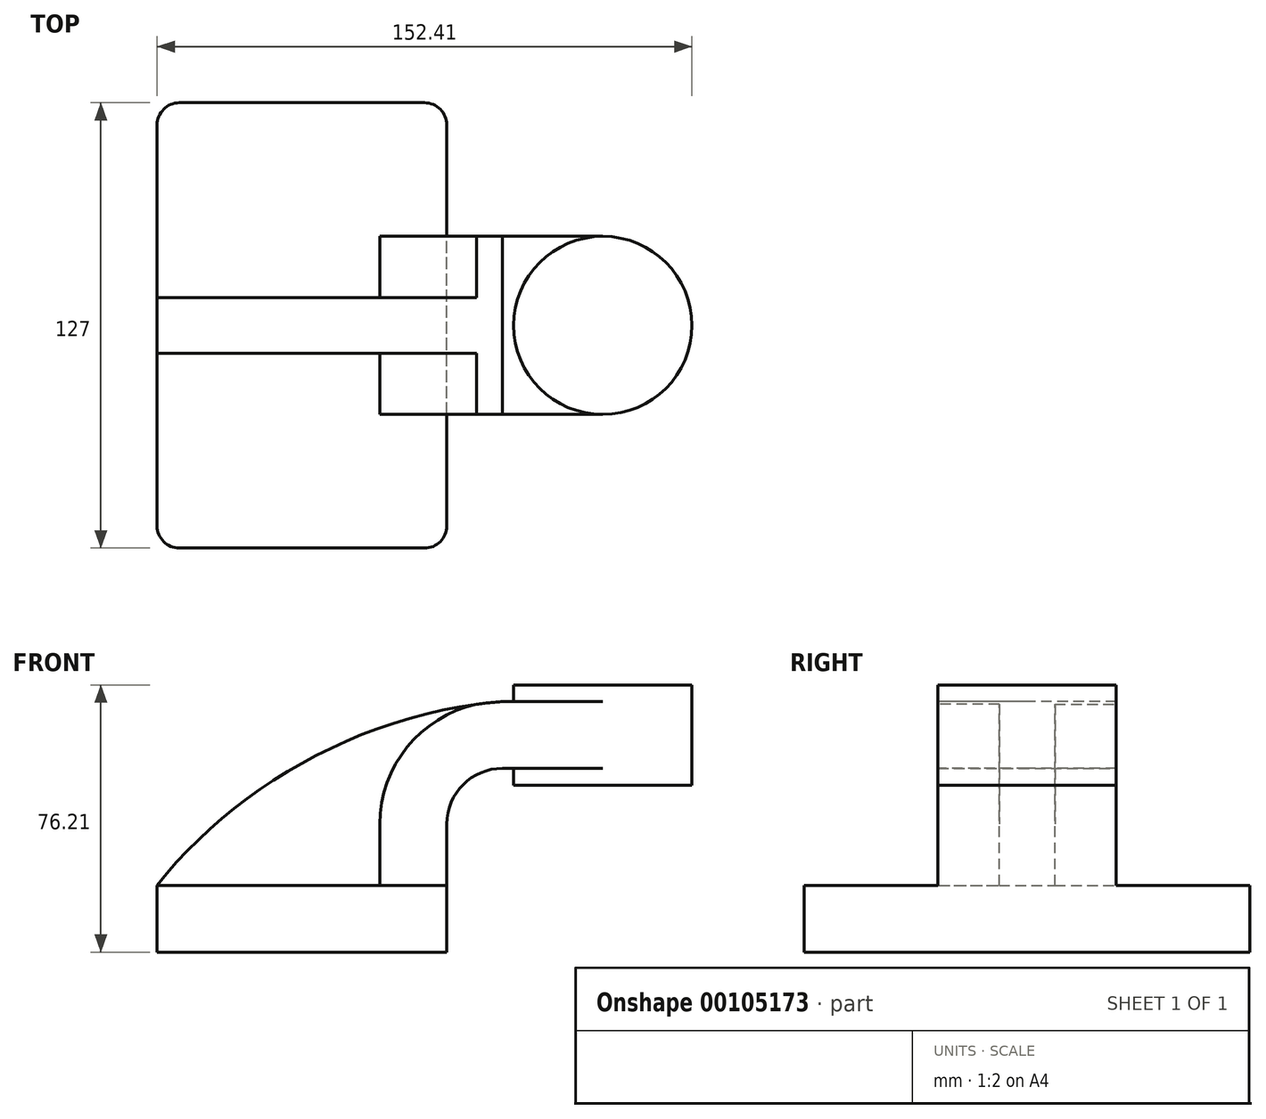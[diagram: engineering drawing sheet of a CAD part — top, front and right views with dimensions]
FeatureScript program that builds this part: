
annotation { "Feature Type Name" : "Feature", "Feature Type Description" : "" }
export const myFeature = defineFeature(function(context is Context, id is Id, definition is map)
    precondition{}
    {
        {
            var Q0;
            Q0=qCreatedBy(makeId("Front.planeOp"),FACE);
            var sketch = newSketch(context, id + "F0", { "sketchPlane" : qUnion([Q0])});
            skLineSegment(sketch, "E0.bottom", {"start": v(41.27, 9.53) * mm, "end": v(-41.28, 9.53) * mm});
            skLineSegment(sketch, "E0.top", {"start": v(41.28, -9.52) * mm, "end": v(-41.27, -9.52) * mm});
            skLineSegment(sketch, "E0.left", {"start": v(41.27, 9.53) * mm, "end": v(41.28, -9.52) * mm});
            skLineSegment(sketch, "E0.right", {"start": v(-41.28, 9.52) * mm, "end": v(-41.27, -9.52) * mm});
            skPoint(sketch, "E0.middle", {"position": v(0, 0) * mm});
            skLineSegment(sketch, "E1.bottom", {"start": v(111.12, 38.1) * mm, "end": v(60.32, 38.1) * mm});
            skLineSegment(sketch, "E1.top", {"start": v(111.12, 66.68) * mm, "end": v(60.32, 66.68) * mm});
            skLineSegment(sketch, "E1.left", {"start": v(111.12, 38.1) * mm, "end": v(111.12, 66.68) * mm});
            skLineSegment(sketch, "E1.right", {"start": v(60.32, 38.1) * mm, "end": v(60.32, 66.68) * mm});
            skPoint(sketch, "E1.middle", {"position": v(85.72, 52.39) * mm});
            skLineSegment(sketch, "E2", {"start": v(41.27, 9.53) * mm, "end": v(41.27, 27) * mm});
            skArc(sketch, "E3", {"start": v(41.27, 27) * mm, "mid": v(45.92, 38.23) * mm, "end": v(57.15, 42.88) * mm});
            skLineSegment(sketch, "E4", {"start": v(57.15, 42.88) * mm, "end": v(85.72, 42.88) * mm});
            skLineSegment(sketch, "E5.0", {"start": v(57.15, 61.93) * mm, "end": v(85.72, 61.93) * mm});
            skArc(sketch, "E5.1", {"start": v(22.22, 27) * mm, "mid": v(32.45, 51.7) * mm, "end": v(57.15, 61.93) * mm});
            skLineSegment(sketch, "E5.2", {"start": v(22.22, 9.53) * mm, "end": v(22.22, 27) * mm});
            skFitSpline(sketch, "E6", {"points": [v(-41.28, 9.52) * mm, v(57.15, 61.93) * mm], "startDerivative": vector(64.97, 82.59) * mm, "endDerivative": vector(120.8, 9.46) * mm});
            skLineSegment(sketch, "E7", {"start": v(85.72, 38.1) * mm, "end": v(85.72, 66.68) * mm});
            skSolve(sketch);
        }
        {
            var Q0;
            Q0=makeQuery(id+"F0.imprint","IMPRINT",FACE,{"disambiguationData":[TD([[makeQuery(id+"F0.imprint","IMPRINT",EDGE,{"derivedFrom":sQuery(id+"F0.wireOp",EDGE,"E0.top")}),-1.0]])]});
            extrude(context, id + "F1", {"entities" : qUnion([Q0]), "endBound" : BoundingType.SYMMETRIC, "depth" : 127 * mm});
        }
        {
            var Q0;
            {var subQ1=sQuery(id+"F0.wireOp",EDGE,"E2");Q0=makeQuery(id+"F0.imprint","IMPRINT",FACE,{"disambiguationData":[TD([[makeQuery(id+"F0.imprint","IMPRINT",EDGE,{"derivedFrom":subQ1}),1.0]])]});}
            var Q1;
            {var subQ5=sQuery(id+"F0.wireOp",EDGE,"Y8enKUxN-u4AB-xJbL-yFZB-ZT1N4Ynt5yWK");Q1=makeQuery(id+"F0.imprint","IMPRINT",FACE,{"disambiguationData":[TD([[makeQuery(id+"F0.imprint","IMPRINT",EDGE,{"derivedFrom":subQ5}),1.0]])]});}
            var Q2;
            {var subQ0=sQuery(id+"F0.wireOp",EDGE,"E4");var subQ1=sQuery(id+"F0.wireOp",EDGE,"E1.right");var subQ2=makeQuery(id+"F0.imprint","INTERSECT",VERTEX,{"derivedFrom":[subQ1,subQ0]});Q2=makeQuery(id+"F0.imprint","IMPRINT",FACE,{"disambiguationData":[TD([[makeQuery(id+"F0.imprint","IMPRINT",EDGE,{"disambiguationData":[TD([[subQ2,-1.0]])],"derivedFrom":subQ1}),-1.0]])]});}
            extrude(context, id + "F2", {"entities" : qUnion([Q0, Q1, Q2]), "operationType" : NewBodyOperationType.ADD, "endBound" : BoundingType.SYMMETRIC, "depth" : 50.8 * mm});
        }
        {
            var Q0;
            {var subQ3=sQuery(id+"F0.wireOp",EDGE,"E5.2");Q0=makeQuery(id+"F0.imprint","IMPRINT",FACE,{"disambiguationData":[TD([[makeQuery(id+"F0.imprint","IMPRINT",EDGE,{"derivedFrom":subQ3}),1.0]])]});}
            extrude(context, id + "F3", {"entities" : qUnion([Q0]), "operationType" : NewBodyOperationType.ADD, "endBound" : BoundingType.SYMMETRIC, "depth" : 15.88 * mm});
        }
        {
            var Q0;
            {var subQ4=sQuery(id+"F0.wireOp",EDGE,"E1.left");Q0=makeQuery(id+"F0.imprint","IMPRINT",FACE,{"disambiguationData":[TD([[makeQuery(id+"F0.imprint","IMPRINT",EDGE,{"derivedFrom":subQ4}),1.0]])]});}
            var Q1;
            Q1=sQuery(id+"F0.wireOp",EDGE,"E7");
            revolve(context, id + "F4", {"operationType" : NewBodyOperationType.ADD, "entities" : qUnion([Q0]), "axis" : qUnion([Q1]), "revolveType" : RevolveType.FULL});
        }
        {
            var Q0;
            Q0=makeQuery(id+"F1.opExtrude","CAP_EDGE",EDGE,{"disambiguationData":[OSD([sQuery(id+"F0.wireOp",EDGE,"E0.left")])],"isStart":false});
            var Q1;
            Q1=makeQuery(id+"F1.opExtrude","CAP_EDGE",EDGE,{"disambiguationData":[OSD([sQuery(id+"F0.wireOp",EDGE,"E0.left")])],"isStart":true});
            var Q2;
            Q2=makeQuery(id+"F1.opExtrude","CAP_EDGE",EDGE,{"disambiguationData":[OSD([sQuery(id+"F0.wireOp",EDGE,"E0.right")])],"isStart":true});
            var Q3;
            Q3=makeQuery(id+"F1.opExtrude","CAP_EDGE",EDGE,{"disambiguationData":[OSD([sQuery(id+"F0.wireOp",EDGE,"E0.right")])],"isStart":false});
            fillet(context, id + "F5", {"entities" : qUnion([Q0, Q1, Q2, Q3]), "radius" : 6.35 * mm, "tangentPropagation" : true, "allowEdgeOverflow" : false});
        }
    });
